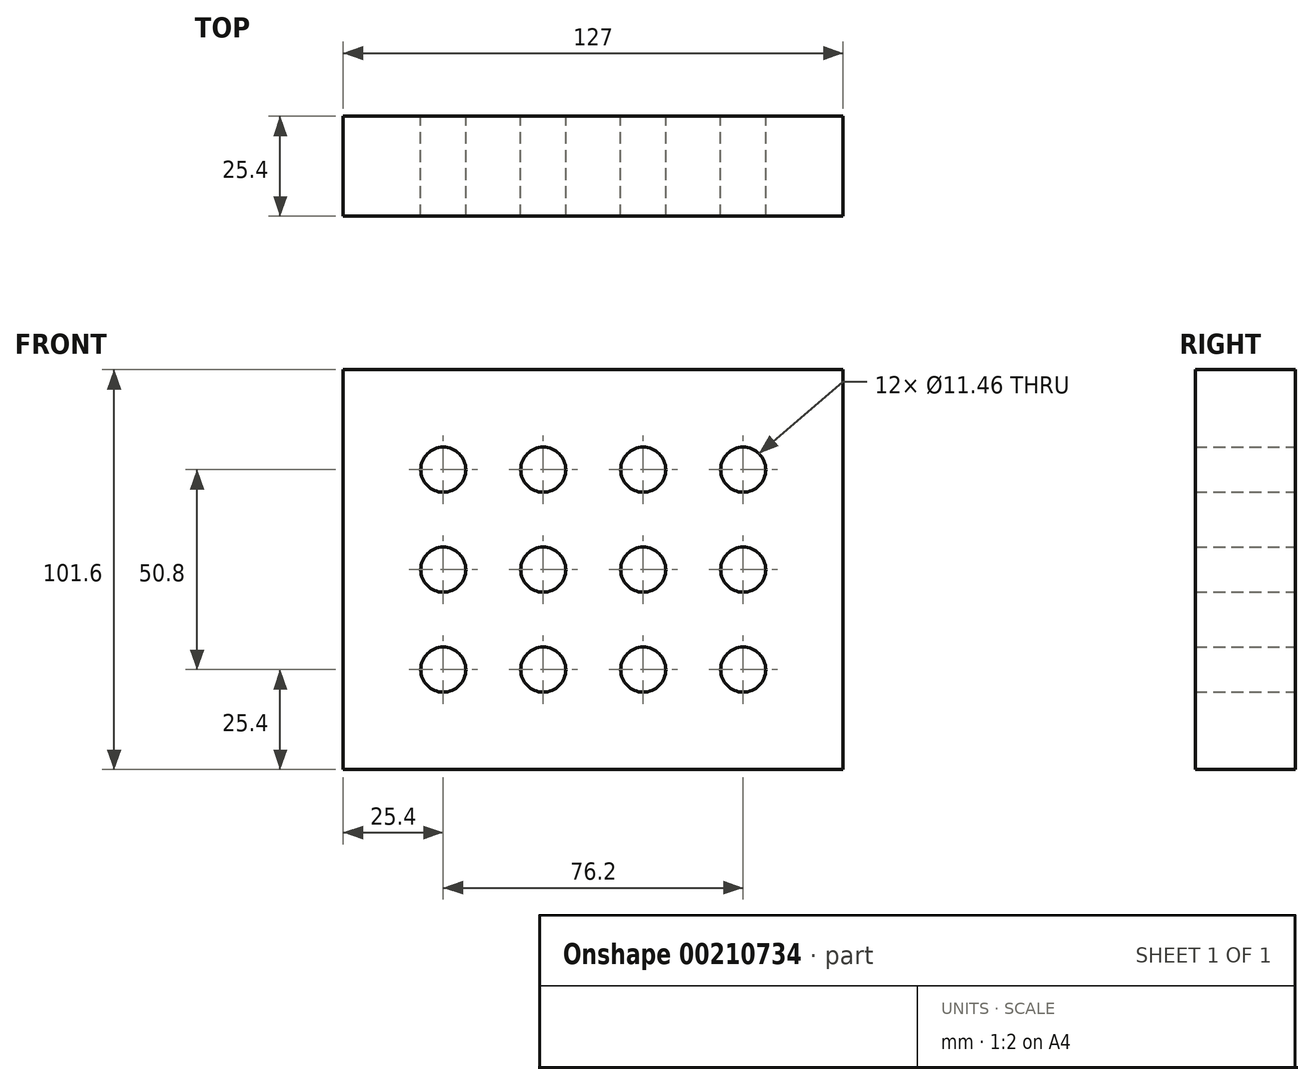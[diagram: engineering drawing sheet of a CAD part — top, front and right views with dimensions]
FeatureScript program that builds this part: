
annotation { "Feature Type Name" : "Feature", "Feature Type Description" : "" }
export const myFeature = defineFeature(function(context is Context, id is Id, definition is map)
    precondition{}
    {
        {
            var Q0;
            Q0=qCreatedBy(makeId("Front.planeOp"),FACE);
            var sketch = newSketch(context, id + "F0", { "sketchPlane" : qUnion([Q0])});
            skLineSegment(sketch, "E0.bottom", {"start": v(-63.5, 50.8) * mm, "end": v(63.5, 50.8) * mm});
            skLineSegment(sketch, "E0.top", {"start": v(-63.5, -50.8) * mm, "end": v(63.5, -50.8) * mm});
            skLineSegment(sketch, "E0.left", {"start": v(-63.5, 50.8) * mm, "end": v(-63.5, -50.8) * mm});
            skLineSegment(sketch, "E0.right", {"start": v(63.5, 50.8) * mm, "end": v(63.5, -50.8) * mm});
            skLineSegment(sketch, "E1.bottom", {"start": v(-38.1, 25.4) * mm, "end": v(38.1, 25.4) * mm});
            skLineSegment(sketch, "E1.top", {"start": v(-38.1, -25.4) * mm, "end": v(38.1, -25.4) * mm});
            skLineSegment(sketch, "E1.left", {"start": v(-38.1, 25.4) * mm, "end": v(-38.1, -25.4) * mm});
            skLineSegment(sketch, "E1.right", {"start": v(38.1, 25.4) * mm, "end": v(38.1, -25.4) * mm});
            skCircle(sketch, "E2", {"center": v(-38.1, 25.4) * mm, "radius": 5.73 * mm});
            skCircle(sketch, "E3", {"center": v(-38.1, 0) * mm, "radius": 5.73 * mm});
            skCircle(sketch, "E4", {"center": v(-38.1, -25.4) * mm, "radius": 5.73 * mm});
            skCircle(sketch, "E5.1.0.0", {"center": v(-12.7, 25.4) * mm, "radius": 5.73 * mm});
            skCircle(sketch, "E5.1.0.1", {"center": v(-12.7, 0) * mm, "radius": 5.73 * mm});
            skCircle(sketch, "E5.1.0.2", {"center": v(-12.7, -25.4) * mm, "radius": 5.73 * mm});
            skCircle(sketch, "E5.2.0.0", {"center": v(12.7, 25.4) * mm, "radius": 5.73 * mm});
            skCircle(sketch, "E5.2.0.1", {"center": v(12.7, 0) * mm, "radius": 5.73 * mm});
            skCircle(sketch, "E5.2.0.2", {"center": v(12.7, -25.4) * mm, "radius": 5.73 * mm});
            skCircle(sketch, "E5.3.0.0", {"center": v(38.1, 25.4) * mm, "radius": 5.73 * mm});
            skCircle(sketch, "E5.3.0.1", {"center": v(38.1, 0) * mm, "radius": 5.73 * mm});
            skCircle(sketch, "E5.3.0.2", {"center": v(38.1, -25.4) * mm, "radius": 5.73 * mm});
            skLineSegment(sketch, "E5.direction1", {"start": v(-38.1, 25.4) * mm, "end": v(-12.7, 25.4) * mm, "construction": true});
            skSolve(sketch);
        }
        {
            var Q0;
            Q0 = qSketchRegion(id + "F0", true);
            var Q1;
            Q1=makeQuery(id+"F0.imprint","IMPRINT",FACE,{"disambiguationData":[TD([[makeQuery(id+"F0.imprint","IMPRINT",EDGE,{"derivedFrom":sQuery(id+"F0.wireOp",EDGE,"E5.1.0.1")}),-1.0]])]});
            extrude(context, id + "F1", {"entities" : qUnion([Q0, Q1]), "depth" : 25.4 * mm});
        }
    });
